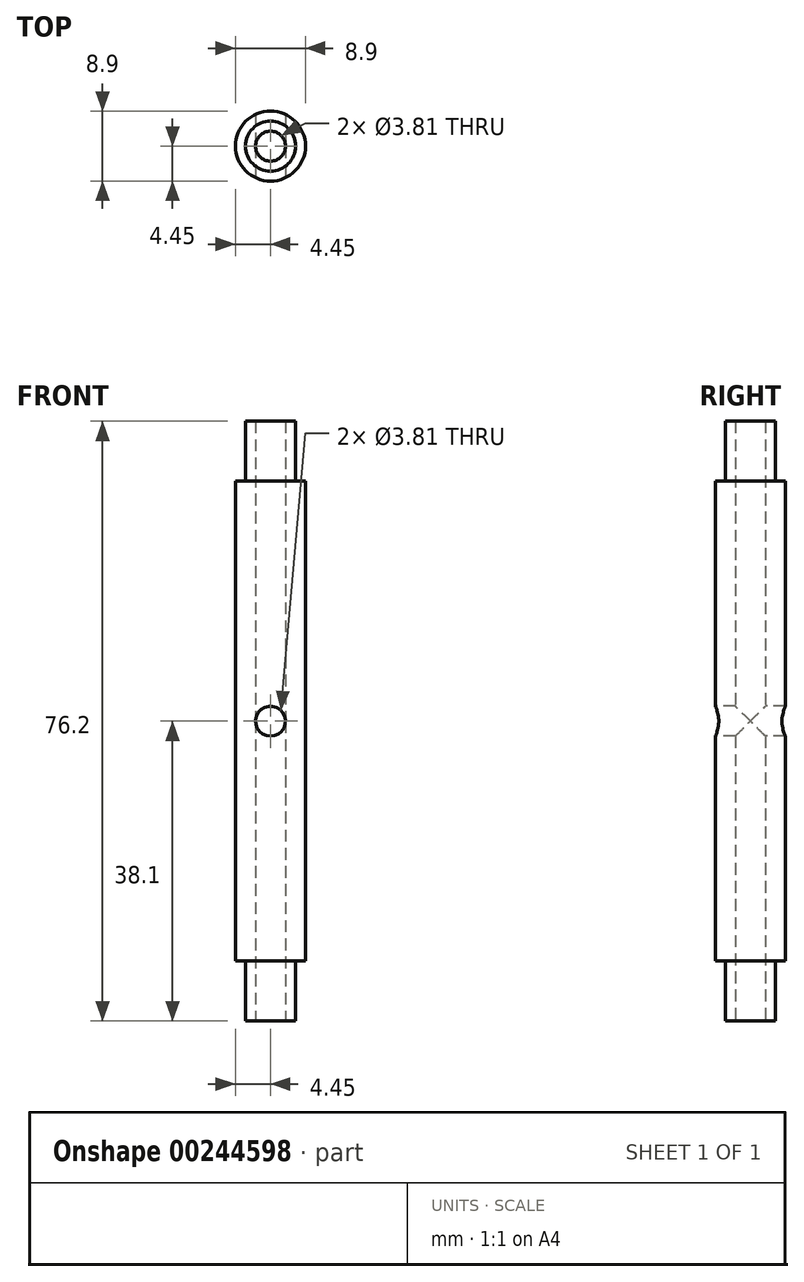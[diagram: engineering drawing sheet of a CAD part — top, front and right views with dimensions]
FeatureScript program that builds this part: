
annotation { "Feature Type Name" : "Feature", "Feature Type Description" : "" }
export const myFeature = defineFeature(function(context is Context, id is Id, definition is map)
    precondition{}
    {
        {
            var Q0;
            Q0=qCreatedBy(makeId("Top.planeOp"),FACE);
            var sketch = newSketch(context, id + "F0", { "sketchPlane" : qUnion([Q0])});
            skCircle(sketch, "E0", {"center": v(0, 0) * mm, "radius": 3.18 * mm});
            skSolve(sketch);
        }
        {
            var Q0;
            Q0=qSketchRegion(id+"F0",true);
            extrude(context, id + "F1", {"entities" : qUnion([Q0]), "depth" : 7.62 * mm});
        }
        {
            var Q0;
            Q0=makeQuery(id+"F1.opExtrude","CAP_FACE",FACE,{"disambiguationData":[OSD([sQuery(id+"F0.wireOp",EDGE,"E0")])],"isStart":false});
            var sketch = newSketch(context, id + "F2", { "sketchPlane" : qUnion([Q0])});
            skCircle(sketch, "E1", {"center": v(0, 0) * mm, "radius": 4.45 * mm});
            skSolve(sketch);
        }
        {
            var Q0;
            Q0=qSketchRegion(id+"F2",true);
            extrude(context, id + "F3", {"entities" : qUnion([Q0]), "operationType" : NewBodyOperationType.ADD, "depth" : 60.96 * mm});
        }
        {
            var Q0;
            Q0=makeQuery(id+"F3.opExtrude","CAP_FACE",FACE,{"disambiguationData":[OSD([sQuery(id+"F2.wireOp",EDGE,"E1")])],"isStart":false});
            var sketch = newSketch(context, id + "F4", { "sketchPlane" : qUnion([Q0])});
            skCircle(sketch, "E2", {"center": v(0, 0) * mm, "radius": 3.18 * mm});
            skSolve(sketch);
        }
        {
            var Q0;
            Q0=qSketchRegion(id+"F4",true);
            extrude(context, id + "F5", {"entities" : qUnion([Q0]), "operationType" : NewBodyOperationType.ADD, "depth" : 7.62 * mm});
        }
        {
            var Q0;
            Q0=qCreatedBy(makeId("Front.planeOp"),FACE);
            var sketch = newSketch(context, id + "F6", { "sketchPlane" : qUnion([Q0])});
            skCircle(sketch, "E3", {"center": v(0, 38.1) * mm, "radius": 1.9 * mm});
            skSolve(sketch);
        }
        {
            var Q0;
            Q0=qSketchRegion(id+"F6",true);
            extrude(context, id + "F7", {"entities" : qUnion([Q0]), "operationType" : NewBodyOperationType.REMOVE, "oppositeDirection" : true, "depth" : 25.4 * mm, "hasSecondDirection" : true, "secondDirectionOppositeDirection" : false, "secondDirectionDepth" : 25.4 * mm});
        }
        {
            var Q0;
            Q0=makeQuery(id+"F1.opExtrude","CAP_FACE",FACE,{"disambiguationData":[OSD([sQuery(id+"F0.wireOp",EDGE,"E0")])],"isStart":true});
            var sketch = newSketch(context, id + "F8", { "sketchPlane" : qUnion([Q0])});
            skCircle(sketch, "E4", {"center": v(0, 0) * mm, "radius": 1.9 * mm});
            skSolve(sketch);
        }
        {
            var Q0;
            Q0=qSketchRegion(id+"F8",true);
            extrude(context, id + "F9", {"entities" : qUnion([Q0]), "operationType" : NewBodyOperationType.REMOVE, "endBound" : BoundingType.THROUGH_ALL, "oppositeDirection" : true, "depth" : 25.4 * mm});
        }
    });
